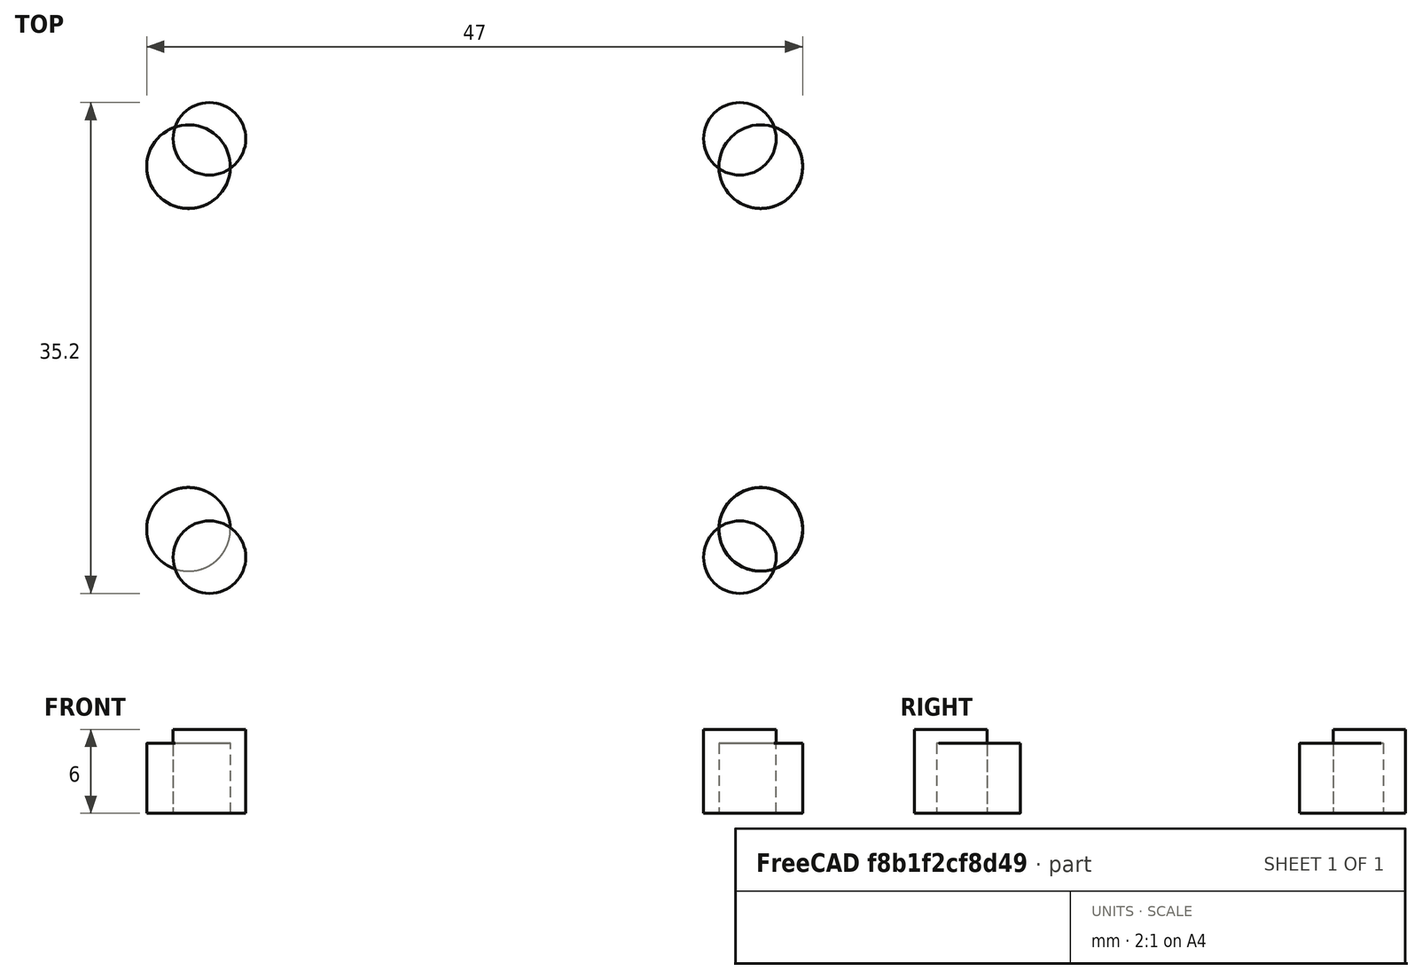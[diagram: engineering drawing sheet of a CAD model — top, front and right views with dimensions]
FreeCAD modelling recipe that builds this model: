
FCSTD DOCUMENT  (FreeCAD 0.14R3702 (Git))
Label: arm
License: CC-BY 3.0
LicenseURL: http://creativecommons.org/licenses/by/3.0/
objects: Sketcher::SketchObject×2, PartDesign::Pad×2, Part::Feature×1, Part::MultiFuse×1
note: 8 computed .brp shape members not serialized (recipe doc carries the construction recipe); baked Part::Feature solids carry a one-line shape summary decoded from their .brp

FEATURE [Sketcher::SketchObject] Sketch
  sketch-geometry (4):
    g0: Circle CenterX=-20.5 CenterY=13 CenterZ=0 NormalX=0 NormalY=0 NormalZ=1 Radius=3
    g1: Circle CenterX=20.5 CenterY=13 CenterZ=0 NormalX=0 NormalY=0 NormalZ=1 Radius=3
    g2: Circle CenterX=-20.5 CenterY=-13 CenterZ=0 NormalX=0 NormalY=0 NormalZ=1 Radius=3
    g3: Circle CenterX=20.5 CenterY=-13 CenterZ=0 NormalX=0 NormalY=0 NormalZ=1 Radius=3
  constraints (9):
    c: Equal(g1,g3)
    c: Equal(g3,g2)
    c: Equal(g2,g0)
    c: Symmetric(g1,g3,g-1)
    c: Symmetric(g0,g2,g-1)
    c: Symmetric(g0,g1,g-2)
    c: DistanceX(g1,g0) = -41
    c: DistanceY(g1,g3) = -26
    c: Radius(g1) = 3
FEATURE [Sketcher::SketchObject] Sketch001
  sketch-geometry (4):
    g0: Circle CenterX=-19 CenterY=15 CenterZ=0 NormalX=0 NormalY=0 NormalZ=1 Radius=2.6
    g1: Circle CenterX=19 CenterY=15 CenterZ=0 NormalX=0 NormalY=0 NormalZ=1 Radius=2.6
    g2: Circle CenterX=-19 CenterY=-15 CenterZ=0 NormalX=0 NormalY=0 NormalZ=1 Radius=2.6
    g3: Circle CenterX=19 CenterY=-15 CenterZ=0 NormalX=0 NormalY=0 NormalZ=1 Radius=2.6
  constraints (9):
    c: Equal(g1,g3)
    c: Equal(g3,g2)
    c: Equal(g2,g0)
    c: Symmetric(g1,g3,g-1)
    c: Symmetric(g0,g2,g-1)
    c: Symmetric(g0,g1,g-2)
    c: DistanceX(g1,g0) = -38
    c: DistanceY(g1,g3) = -30
    c: Radius(g1) = 2.6
FEATURE [PartDesign::Pad] Pad
  Length = 5
  Length2 = 100
  Sketch = -> Sketch
  Type = 0
FEATURE [PartDesign::Pad] Pad001
  Length = 6
  Length2 = 100
  Sketch = -> Sketch001
  Type = 0
FEATURE [Part::Feature] mk3_car_arm_anti_backlash001_solid  label="mk3_car_arm_anti_backlash001 (Solid)"
  shape: bbox 61 x 46 x 99.8 mm, 17362 faces (baked)
FEATURE [Part::MultiFuse] Fusion
  Shapes = -> [Pad,mk3_car_arm_anti_backlash001_solid]
